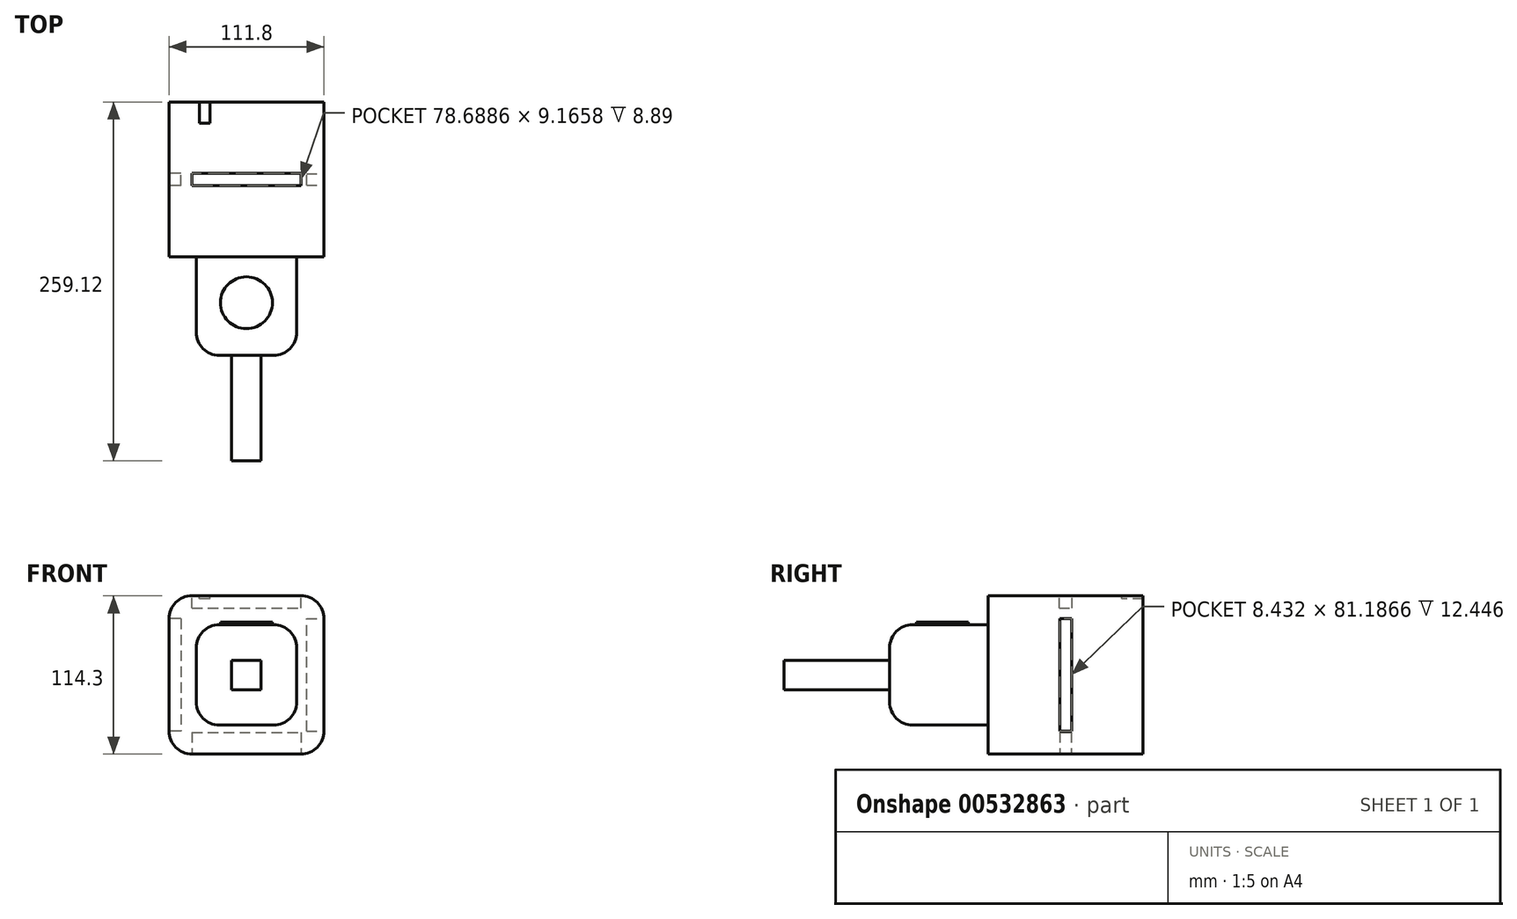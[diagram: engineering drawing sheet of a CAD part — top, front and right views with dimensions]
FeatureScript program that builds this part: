
annotation { "Feature Type Name" : "Feature", "Feature Type Description" : "" }
export const myFeature = defineFeature(function(context is Context, id is Id, definition is map)
    precondition{}
    {
        {
            var Q0;
            Q0=qCreatedBy(makeId("Top.planeOp"),FACE);
            var sketch = newSketch(context, id + "F0", { "sketchPlane" : qUnion([Q0])});
            skLineSegment(sketch, "E0.bottom", {"start": v(55.9, -55.9) * mm, "end": v(-55.9, -55.9) * mm});
            skLineSegment(sketch, "E0.top", {"start": v(55.9, 55.9) * mm, "end": v(-55.9, 55.9) * mm});
            skLineSegment(sketch, "E0.left", {"start": v(55.9, -55.9) * mm, "end": v(55.9, 55.9) * mm});
            skLineSegment(sketch, "E0.right", {"start": v(-55.9, -55.9) * mm, "end": v(-55.9, 55.9) * mm});
            skPoint(sketch, "E0.middle", {"position": v(0, 0) * mm});
            skSolve(sketch);
        }
        {
            var Q0;
            Q0 = qSketchRegion(id + "F0", true);
            extrude(context, id + "F1", {"entities" : qUnion([Q0]), "endBound" : BoundingType.SYMMETRIC, "depth" : 114.3 * mm, "offsetDistance" : 25.4 * mm});
        }
        {
            var Q0;
            Q0=makeQuery(id+"F1.opExtrude","SWEPT_FACE",FACE,{"disambiguationData":[OSD([sQuery(id+"F0.wireOp",EDGE,"E0.bottom")])]});
            var sketch = newSketch(context, id + "F2", { "sketchPlane" : qUnion([Q0])});
            skLineSegment(sketch, "E1.bottom", {"start": v(36.24, -36.24) * mm, "end": v(-36.24, -36.24) * mm});
            skLineSegment(sketch, "E1.top", {"start": v(36.24, 36.24) * mm, "end": v(-36.24, 36.24) * mm});
            skLineSegment(sketch, "E1.left", {"start": v(36.24, -36.24) * mm, "end": v(36.24, 36.24) * mm});
            skLineSegment(sketch, "E1.right", {"start": v(-36.24, -36.24) * mm, "end": v(-36.24, 36.24) * mm});
            skPoint(sketch, "E1.middle", {"position": v(0, 0) * mm});
            skSolve(sketch);
        }
        {
            var Q0;
            Q0 = qSketchRegion(id + "F2", true);
            extrude(context, id + "F3", {"entities" : qUnion([Q0]), "operationType" : NewBodyOperationType.ADD, "depth" : 71.12 * mm, "offsetDistance" : 25.4 * mm});
        }
        {
            var Q0;
            Q0=makeQuery(id+"F3.opExtrude","CAP_FACE",FACE,{"disambiguationData":[OSD([sQuery(id+"F2.wireOp",EDGE,"E1.bottom"),sQuery(id+"F2.wireOp",EDGE,"E1.top"),sQuery(id+"F2.wireOp",EDGE,"E1.left"),sQuery(id+"F2.wireOp",EDGE,"E1.right")])],"isStart":false});
            var sketch = newSketch(context, id + "F4", { "sketchPlane" : qUnion([Q0])});
            skLineSegment(sketch, "E2.bottom", {"start": v(10.6, -10.6) * mm, "end": v(-10.6, -10.6) * mm});
            skLineSegment(sketch, "E2.top", {"start": v(10.6, 10.6) * mm, "end": v(-10.6, 10.6) * mm});
            skLineSegment(sketch, "E2.left", {"start": v(10.6, -10.6) * mm, "end": v(10.6, 10.6) * mm});
            skLineSegment(sketch, "E2.right", {"start": v(-10.6, -10.6) * mm, "end": v(-10.6, 10.6) * mm});
            skPoint(sketch, "E2.middle", {"position": v(0, 0) * mm});
            skSolve(sketch);
        }
        {
            var Q0;
            Q0 = qSketchRegion(id + "F4", true);
            extrude(context, id + "F5", {"entities" : qUnion([Q0]), "operationType" : NewBodyOperationType.ADD, "depth" : 76.2 * mm, "offsetDistance" : 25.4 * mm});
        }
        {
            var Q0;
            Q0=makeQuery(id+"F1.opExtrude","CAP_EDGE",EDGE,{"disambiguationData":[OSD([sQuery(id+"F0.wireOp",EDGE,"E0.right")])],"isStart":false});
            var Q1;
            Q1=makeQuery(id+"F1.opExtrude","CAP_EDGE",EDGE,{"disambiguationData":[OSD([sQuery(id+"F0.wireOp",EDGE,"E0.right")])],"isStart":true});
            var Q2;
            Q2=makeQuery(id+"F1.opExtrude","CAP_EDGE",EDGE,{"disambiguationData":[OSD([sQuery(id+"F0.wireOp",EDGE,"E0.left")])],"isStart":true});
            var Q3;
            Q3=makeQuery(id+"F1.opExtrude","CAP_EDGE",EDGE,{"disambiguationData":[OSD([sQuery(id+"F0.wireOp",EDGE,"E0.left")])],"isStart":false});
            var Q4;
            Q4=makeQuery(id+"F3.opExtrude","CAP_EDGE",EDGE,{"disambiguationData":[OSD([sQuery(id+"F2.wireOp",EDGE,"E1.left")])],"isStart":false});
            var Q5;
            Q5=makeQuery(id+"F3.opExtrude","CAP_EDGE",EDGE,{"disambiguationData":[OSD([sQuery(id+"F2.wireOp",EDGE,"E1.bottom")])],"isStart":false});
            var Q6;
            Q6=makeQuery(id+"F3.opExtrude","CAP_EDGE",EDGE,{"disambiguationData":[OSD([sQuery(id+"F2.wireOp",EDGE,"E1.right")])],"isStart":false});
            var Q7;
            Q7=makeQuery(id+"F3.opExtrude","CAP_EDGE",EDGE,{"disambiguationData":[OSD([sQuery(id+"F2.wireOp",EDGE,"E1.top")])],"isStart":false});
            var Q8;
            Q8=makeQuery(id+"F3.opExtrude","SWEPT_EDGE",EDGE,{"disambiguationData":[OSD([sQuery(id+"F2.wireOp",EDGE,"E1.bottom"),sQuery(id+"F2.wireOp",EDGE,"E1.right")])]});
            var Q9;
            Q9=makeQuery(id+"F3.opExtrude","SWEPT_EDGE",EDGE,{"disambiguationData":[OSD([sQuery(id+"F2.wireOp",EDGE,"E1.bottom"),sQuery(id+"F2.wireOp",EDGE,"E1.left")])]});
            var Q10;
            Q10=makeQuery(id+"F3.opExtrude","SWEPT_EDGE",EDGE,{"disambiguationData":[OSD([sQuery(id+"F2.wireOp",EDGE,"E1.top"),sQuery(id+"F2.wireOp",EDGE,"E1.left")])]});
            var Q11;
            Q11=makeQuery(id+"F3.opExtrude","SWEPT_EDGE",EDGE,{"disambiguationData":[OSD([sQuery(id+"F2.wireOp",EDGE,"E1.top"),sQuery(id+"F2.wireOp",EDGE,"E1.right")])]});
            fillet(context, id + "F6", {"entities" : qUnion([Q0, Q1, Q2, Q3, Q4, Q5, Q6, Q7, Q8, Q9, Q10, Q11]), "radius" : 16.56 * mm, "tangentPropagation" : true, "allowEdgeOverflow" : false});
        }
        {
            var Q0;
            Q0=makeQuery(id+"F1.opExtrude","CAP_FACE",FACE,{"disambiguationData":[OSD([sQuery(id+"F0.wireOp",EDGE,"E0.bottom"),sQuery(id+"F0.wireOp",EDGE,"E0.top"),sQuery(id+"F0.wireOp",EDGE,"E0.left"),sQuery(id+"F0.wireOp",EDGE,"E0.right")])],"isStart":false});
            var sketch = newSketch(context, id + "F7", { "sketchPlane" : qUnion([Q0])});
            skLineSegment(sketch, "E3.bottom", {"start": v(-33.99, 55.9) * mm, "end": v(-26.35, 55.9) * mm});
            skLineSegment(sketch, "E3.top", {"start": v(-33.99, 40.48) * mm, "end": v(-26.35, 40.48) * mm});
            skLineSegment(sketch, "E3.left", {"start": v(-33.99, 55.9) * mm, "end": v(-33.99, 40.48) * mm});
            skLineSegment(sketch, "E3.right", {"start": v(-26.35, 55.9) * mm, "end": v(-26.35, 40.48) * mm});
            skSolve(sketch);
        }
        {
            var Q0;
            Q0 = qSketchRegion(id + "F7", true);
            extrude(context, id + "F8", {"entities" : qUnion([Q0]), "operationType" : NewBodyOperationType.ADD, "depth" : 25.4 * mm, "offsetDistance" : 25.4 * mm});
        }
        {
            var Q0;
            Q0=makeQuery(id+"F8.opExtrude","CAP_FACE",FACE,{"disambiguationData":[OSD([sQuery(id+"F7.wireOp",EDGE,"E3.bottom"),sQuery(id+"F7.wireOp",EDGE,"E3.top"),sQuery(id+"F7.wireOp",EDGE,"E3.left"),sQuery(id+"F7.wireOp",EDGE,"E3.right")])],"isStart":false});
            extrude(context, id + "F9", {"entities" : qUnion([Q0]), "operationType" : NewBodyOperationType.REMOVE, "oppositeDirection" : true, "depth" : 27.43 * mm, "offsetDistance" : 25.4 * mm});
        }
        {
            var Q0;
            Q0=makeQuery(id+"F1.opExtrude","CAP_FACE",FACE,{"disambiguationData":[OSD([sQuery(id+"F0.wireOp",EDGE,"E0.bottom"),sQuery(id+"F0.wireOp",EDGE,"E0.top"),sQuery(id+"F0.wireOp",EDGE,"E0.left"),sQuery(id+"F0.wireOp",EDGE,"E0.right")])],"isStart":false});
            var sketch = newSketch(context, id + "F10", { "sketchPlane" : qUnion([Q0])});
            skLineSegment(sketch, "E4.bottom", {"start": v(-39.34, -4.58) * mm, "end": v(39.34, -4.58) * mm});
            skLineSegment(sketch, "E4.top", {"start": v(-39.34, 4.58) * mm, "end": v(39.34, 4.58) * mm});
            skLineSegment(sketch, "E4.left", {"start": v(-39.34, -4.58) * mm, "end": v(-39.34, 4.58) * mm});
            skLineSegment(sketch, "E4.right", {"start": v(39.34, -4.58) * mm, "end": v(39.34, 4.58) * mm});
            skPoint(sketch, "E4.middle", {"position": v(0, 0) * mm});
            skSolve(sketch);
        }
        {
            var Q0;
            Q0 = qSketchRegion(id + "F10", true);
            extrude(context, id + "F11", {"entities" : qUnion([Q0]), "operationType" : NewBodyOperationType.REMOVE, "oppositeDirection" : true, "depth" : 8.9 * mm, "offsetDistance" : 25.4 * mm});
        }
        {
            var Q0;
            Q0=makeQuery(id+"F1.opExtrude","SWEPT_FACE",FACE,{"disambiguationData":[OSD([sQuery(id+"F0.wireOp",EDGE,"E0.right")])]});
            var sketch = newSketch(context, id + "F12", { "sketchPlane" : qUnion([Q0])});
            skLineSegment(sketch, "E5.bottom", {"start": v(4.36, 40.6) * mm, "end": v(-4.36, 40.6) * mm});
            skLineSegment(sketch, "E5.top", {"start": v(4.36, -40.6) * mm, "end": v(-4.36, -40.6) * mm});
            skLineSegment(sketch, "E5.left", {"start": v(4.36, 40.6) * mm, "end": v(4.36, -40.6) * mm});
            skLineSegment(sketch, "E5.right", {"start": v(-4.36, 40.6) * mm, "end": v(-4.36, -40.6) * mm});
            skPoint(sketch, "E5.middle", {"position": v(0, 0) * mm});
            skSolve(sketch);
        }
        {
            var Q0;
            Q0 = qSketchRegion(id + "F12", true);
            extrude(context, id + "F13", {"entities" : qUnion([Q0]), "operationType" : NewBodyOperationType.REMOVE, "oppositeDirection" : true, "depth" : 8.64 * mm, "offsetDistance" : 25.4 * mm});
        }
        {
            var Q0;
            Q0=makeQuery(id+"F1.opExtrude","CAP_FACE",FACE,{"disambiguationData":[OSD([sQuery(id+"F0.wireOp",EDGE,"E0.bottom"),sQuery(id+"F0.wireOp",EDGE,"E0.top"),sQuery(id+"F0.wireOp",EDGE,"E0.left"),sQuery(id+"F0.wireOp",EDGE,"E0.right")])],"isStart":true});
            var sketch = newSketch(context, id + "F14", { "sketchPlane" : qUnion([Q0])});
            skLineSegment(sketch, "E6.bottom", {"start": v(-39.34, 4.15) * mm, "end": v(39.34, 4.15) * mm});
            skLineSegment(sketch, "E6.top", {"start": v(-39.34, -4.15) * mm, "end": v(39.34, -4.15) * mm});
            skLineSegment(sketch, "E6.left", {"start": v(-39.34, 4.15) * mm, "end": v(-39.34, -4.15) * mm});
            skLineSegment(sketch, "E6.right", {"start": v(39.34, 4.15) * mm, "end": v(39.34, -4.15) * mm});
            skPoint(sketch, "E6.middle", {"position": v(0, 0) * mm});
            skSolve(sketch);
        }
        {
            var Q0;
            Q0 = qSketchRegion(id + "F14", true);
            extrude(context, id + "F15", {"entities" : qUnion([Q0]), "operationType" : NewBodyOperationType.REMOVE, "oppositeDirection" : true, "depth" : 15.75 * mm, "offsetDistance" : 25.4 * mm});
        }
        {
            var Q0;
            Q0=makeQuery(id+"F1.opExtrude","SWEPT_FACE",FACE,{"disambiguationData":[OSD([sQuery(id+"F0.wireOp",EDGE,"E0.left")])]});
            var sketch = newSketch(context, id + "F16", { "sketchPlane" : qUnion([Q0])});
            skLineSegment(sketch, "E7.bottom", {"start": v(-4.22, -40.6) * mm, "end": v(4.22, -40.6) * mm});
            skLineSegment(sketch, "E7.top", {"start": v(-4.22, 40.6) * mm, "end": v(4.22, 40.6) * mm});
            skLineSegment(sketch, "E7.left", {"start": v(-4.22, -40.6) * mm, "end": v(-4.22, 40.6) * mm});
            skLineSegment(sketch, "E7.right", {"start": v(4.22, -40.6) * mm, "end": v(4.22, 40.6) * mm});
            skPoint(sketch, "E7.middle", {"position": v(0, 0) * mm});
            skSolve(sketch);
        }
        {
            var Q0;
            Q0 = qSketchRegion(id + "F16", true);
            extrude(context, id + "F17", {"entities" : qUnion([Q0]), "operationType" : NewBodyOperationType.REMOVE, "oppositeDirection" : true, "depth" : 12.45 * mm, "offsetDistance" : 25.4 * mm});
        }
        {
            var Q0;
            Q0=makeQuery(id+"F3.opExtrude","SWEPT_FACE",FACE,{"disambiguationData":[OSD([sQuery(id+"F2.wireOp",EDGE,"E1.top")])]});
            var sketch = newSketch(context, id + "F18", { "sketchPlane" : qUnion([Q0])});
            skCircle(sketch, "E8", {"center": v(0, -89.05) * mm, "radius": 18.73 * mm});
            skSolve(sketch);
        }
        {
            var Q0;
            Q0 = qSketchRegion(id + "F18", true);
            extrude(context, id + "F19", {"entities" : qUnion([Q0]), "operationType" : NewBodyOperationType.ADD, "depth" : 1.78 * mm, "offsetDistance" : 25.4 * mm});
        }
    });
